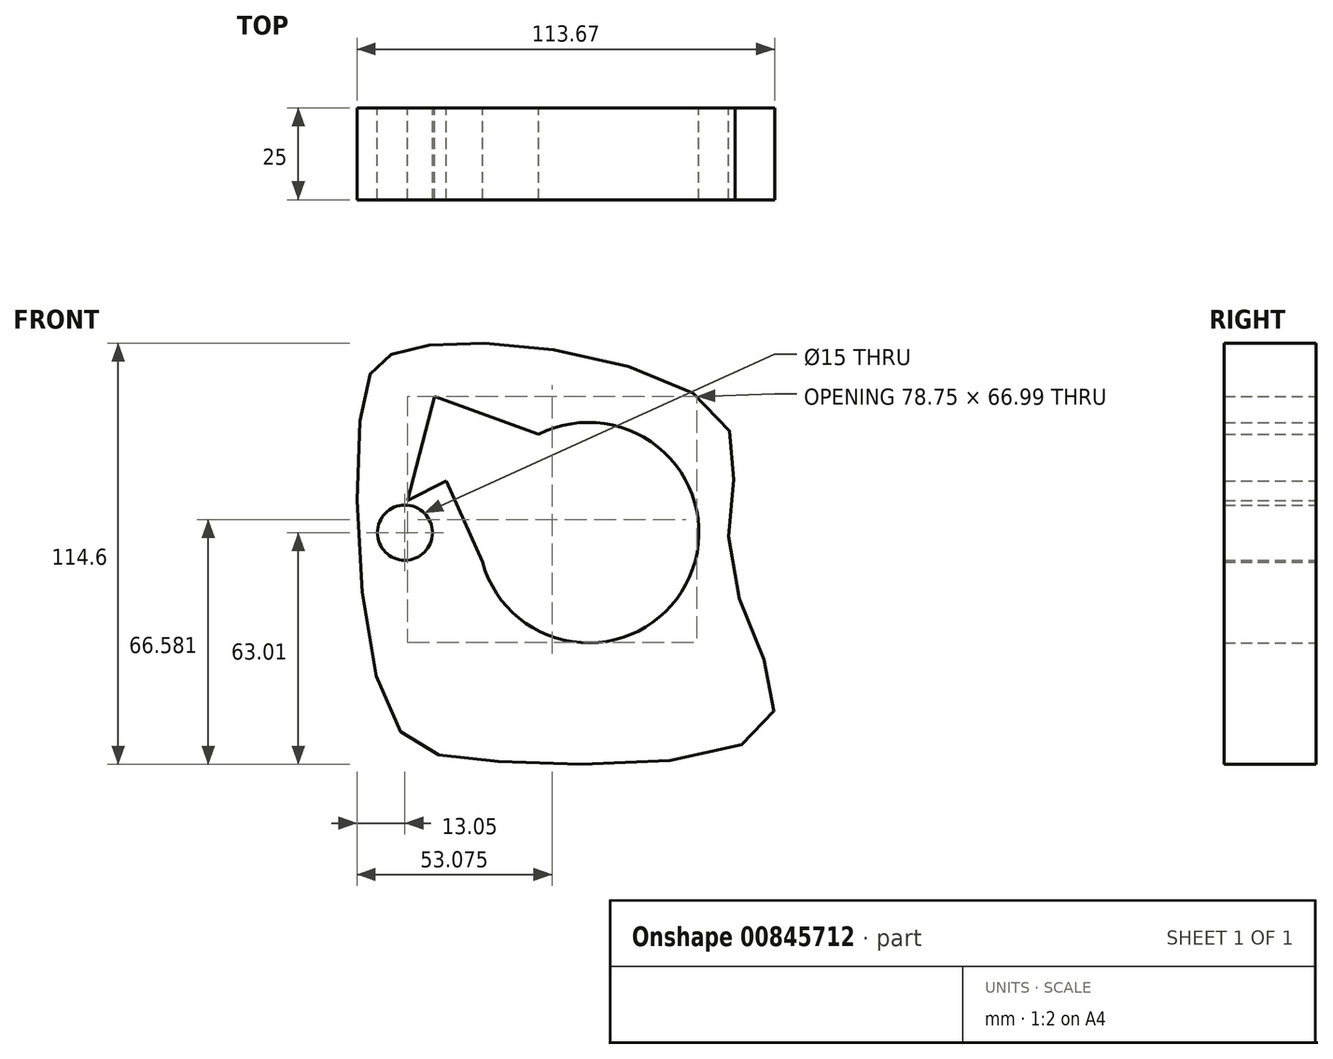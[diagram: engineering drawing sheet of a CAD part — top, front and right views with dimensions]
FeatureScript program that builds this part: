
annotation { "Feature Type Name" : "Feature", "Feature Type Description" : "" }
export const myFeature = defineFeature(function(context is Context, id is Id, definition is map)
    precondition{}
    {
        {
            var Q0;
            Q0=qCreatedBy(makeId("Front.planeOp"),FACE);
            var sketch = newSketch(context, id + "F0", { "sketchPlane" : qUnion([Q0])});
            skCircle(sketch, "E0", {"center": v(0, 0) * mm, "radius": 30 * mm});
            skCircle(sketch, "E1", {"center": v(-50, 0) * mm, "radius": 7.5 * mm});
            skLineSegment(sketch, "E2", {"start": v(-13.6, 26.74) * mm, "end": v(-49.35, 8.73) * mm});
            skLineSegment(sketch, "E3", {"start": v(-49.35, 8.73) * mm, "end": v(-41.99, 37.07) * mm});
            skLineSegment(sketch, "E4", {"start": v(-41.99, 37.07) * mm, "end": v(-13.6, 26.74) * mm});
            skFitSpline(sketch, "E5", {"points": [v(-53.68, 48.45) * mm, v(-19.23, 50.91) * mm, v(37.38, 29.69) * mm, v(38.6, -9.07) * mm, v(49.06, -52.14) * mm, v(-24.76, -62.3) * mm, v(-54.6, -48.45) * mm, v(-61.37, 36.76) * mm, v(-53.68, 48.45) * mm]});
            skLineSegment(sketch, "E6", {"start": v(-42.3, 22) * mm, "end": v(-17.87, -32.8) * mm});
            skSolve(sketch);
        }
        {
            var Q0;
            Q0 = qSketchRegion(id + "F0", true);
            extrude(context, id + "F1", {"entities" : qUnion([Q0]), "depth" : 25 * mm, "offsetDistance" : 25 * mm});
        }
    });
